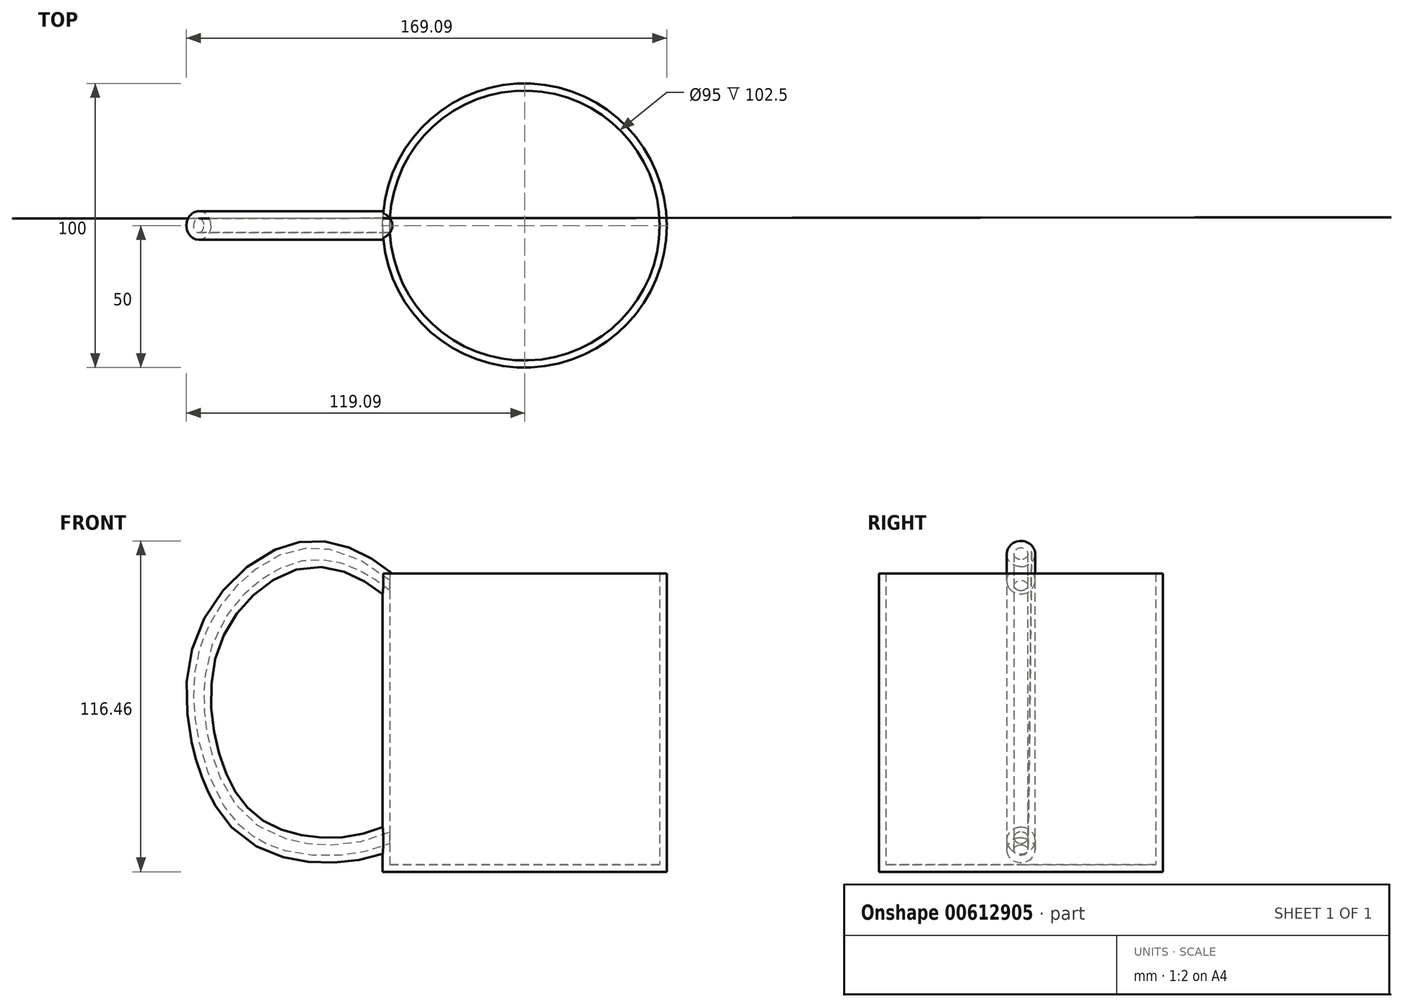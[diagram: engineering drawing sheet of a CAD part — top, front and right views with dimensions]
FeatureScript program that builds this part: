
annotation { "Feature Type Name" : "Feature", "Feature Type Description" : "" }
export const myFeature = defineFeature(function(context is Context, id is Id, definition is map)
    precondition{}
    {
        {
            var Q0;
            Q0=qCreatedBy(makeId("Top.planeOp"),FACE);
            var sketch = newSketch(context, id + "F0", { "sketchPlane" : qUnion([Q0])});
            skCircle(sketch, "E0", {"center": v(0, 0) * mm, "radius": 50 * mm});
            skSolve(sketch);
        }
        {
            var Q0;
            Q0=makeQuery(id+"F0.imprint","IMPRINT",FACE,{"disambiguationData":[TD([[makeQuery(id+"F0.imprint","IMPRINT",EDGE,{"derivedFrom":sQuery(id+"F0.wireOp",EDGE,"E0")}),1.0]])]});
            extrude(context, id + "F1", {"entities" : qUnion([Q0]), "depth" : 105 * mm, "offsetDistance" : 25 * mm});
        }
        {
            var Q0;
            Q0=qCreatedBy(makeId("Front.planeOp"),FACE);
            var sketch = newSketch(context, id + "F2", { "sketchPlane" : qUnion([Q0])});
            skFitSpline(sketch, "E1", {"points": [v(-44.22, 81.5) * mm, v(-72.91, 97.76) * mm, v(-97.76, 78.83) * mm, v(-98.65, 43.33) * mm, v(-86.22, 25.59) * mm, v(-61.97, 21.74) * mm, v(-38, 32.1) * mm], "startDerivative": vector(-156.43, 137.73) * mm, "endDerivative": vector(143.98, 83.41) * mm});
            skSolve(sketch);
        }
        {
            var Q0;
            Q0=qCreatedBy(makeId("Right.planeOp"),FACE);
            cPlane(context, id + "F3", {"entities" : qUnion([Q0]), "cplaneType" : CPlaneType.OFFSET, "offset" : 45 * mm, "oppositeDirection" : true, "width" : 150 * mm, "height" : 150 * mm});
        }
        {
            var Q0;
            Q0=qCreatedBy(id+"F3.planeOp",FACE);
            var sketch = newSketch(context, id + "F4", { "sketchPlane" : qUnion([Q0])});
            skCircle(sketch, "E2", {"center": v(0, 98.67) * mm, "radius": 5 * mm});
            skSolve(sketch);
        }
        {
            var Q0;
            Q0 = qSketchRegion(id + "F4", true);
            var Q1;
            Q1=sQuery(id+"F2.wireOp",EDGE,"E1");
            sweep(context, id + "F5", {"operationType" : NewBodyOperationType.ADD, "profiles" : qUnion([Q0]), "path" : qUnion([Q1])});
        }
        {
            var Q0;
            Q0=makeQuery(id+"F1.opExtrude","CAP_FACE",FACE,{"disambiguationData":[OSD([sQuery(id+"F0.wireOp",EDGE,"E0")])],"isStart":false});
            shell(context, id + "F6", {"entities" : qUnion([Q0]), "thickness" : 2.5 * mm});
        }
    });
